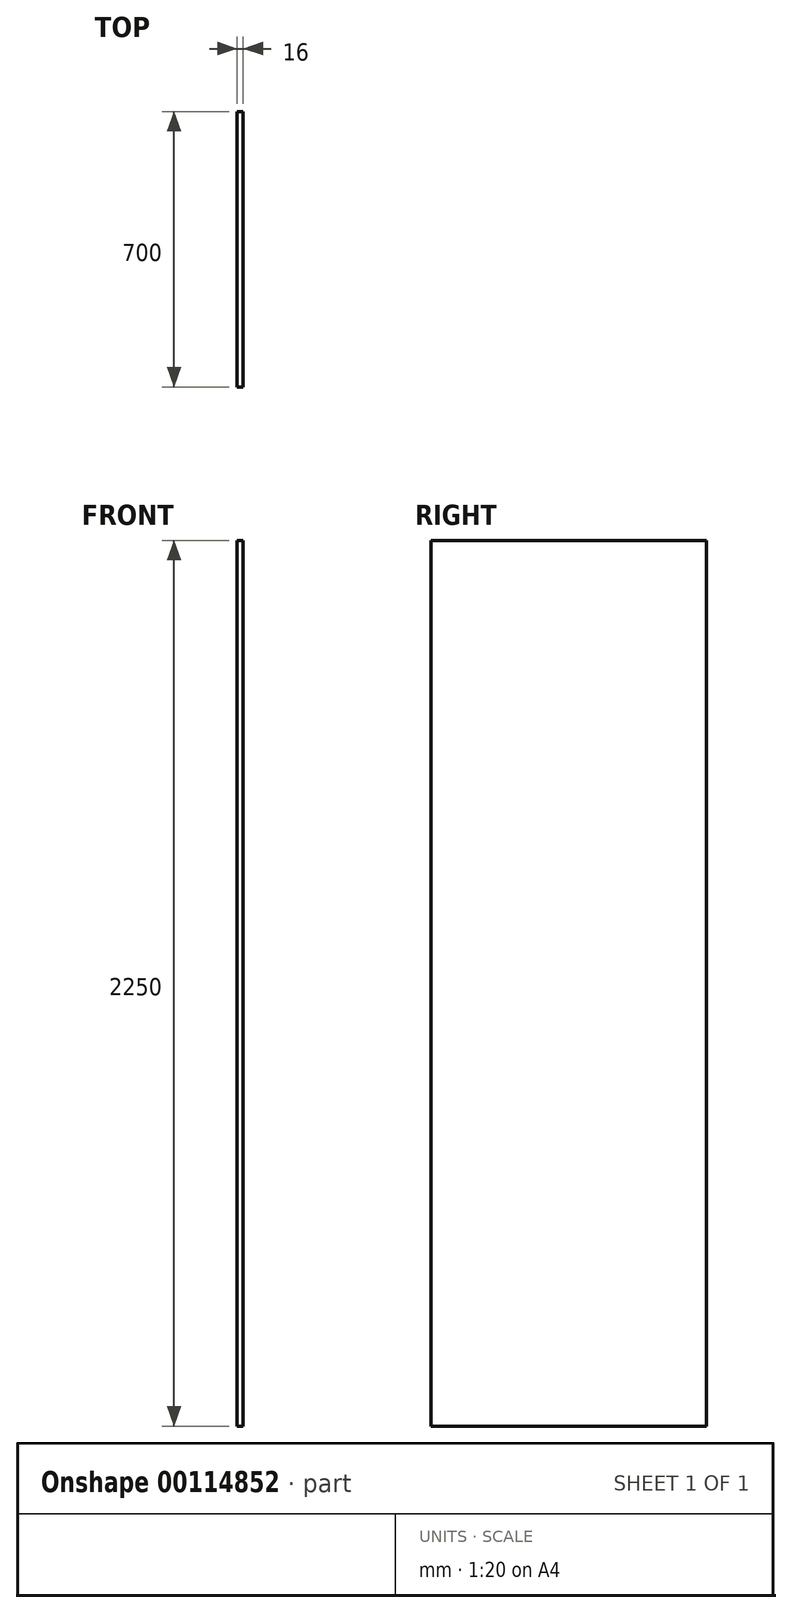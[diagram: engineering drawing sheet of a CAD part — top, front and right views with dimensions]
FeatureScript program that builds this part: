
annotation { "Feature Type Name" : "Feature", "Feature Type Description" : "" }
export const myFeature = defineFeature(function(context is Context, id is Id, definition is map)
    precondition{}
    {
        {
            var Q0;
            Q0=qCreatedBy(makeId("Right.planeOp"),FACE);
            var sketch = newSketch(context, id + "F0", { "sketchPlane" : qUnion([Q0])});
            skLineSegment(sketch, "E0.bottom", {"start": v(-350, -1125) * mm, "end": v(350, -1125) * mm});
            skLineSegment(sketch, "E0.top", {"start": v(-350, 1125) * mm, "end": v(350, 1125) * mm});
            skLineSegment(sketch, "E0.left", {"start": v(-350, -1125) * mm, "end": v(-350, 1125) * mm});
            skLineSegment(sketch, "E0.right", {"start": v(350, -1125) * mm, "end": v(350, 1125) * mm});
            skPoint(sketch, "E0.middle", {"position": v(0, 0) * mm});
            skSolve(sketch);
        }
        {
            var Q0;
            Q0=makeQuery(id+"F0.imprint","IMPRINT",FACE,{"disambiguationData":[TD([[makeQuery(id+"F0.imprint","IMPRINT",EDGE,{"derivedFrom":sQuery(id+"F0.wireOp",EDGE,"E0.bottom")}),1.0]])]});
            extrude(context, id + "F1", {"entities" : qUnion([Q0]), "endBound" : BoundingType.SYMMETRIC, "depth" : 16 * mm});
        }
    });
